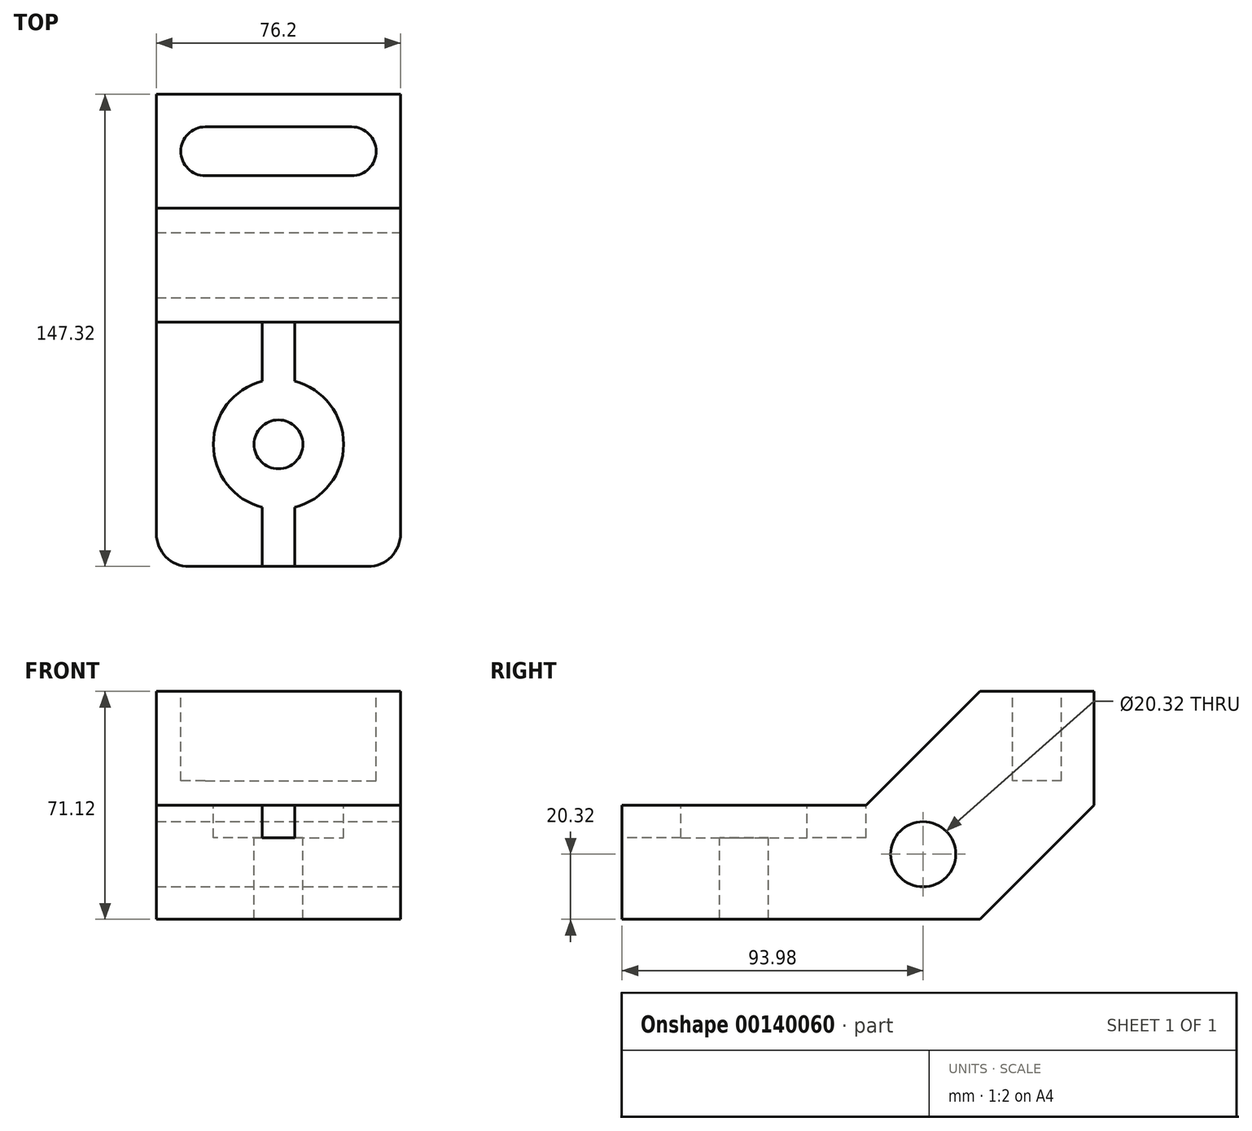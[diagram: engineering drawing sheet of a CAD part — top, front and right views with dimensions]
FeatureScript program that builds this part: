
annotation { "Feature Type Name" : "Feature", "Feature Type Description" : "" }
export const myFeature = defineFeature(function(context is Context, id is Id, definition is map)
    precondition{}
    {
        {
            var Q0;
            Q0=qCreatedBy(makeId("Right.planeOp"),FACE);
            var sketch = newSketch(context, id + "F0", { "sketchPlane" : qUnion([Q0])});
            skLineSegment(sketch, "E0", {"start": v(0, 0) * mm, "end": v(0, 35.56) * mm});
            skLineSegment(sketch, "E1", {"start": v(0, 35.56) * mm, "end": v(76.2, 35.56) * mm});
            skLineSegment(sketch, "E2", {"start": v(76.2, 35.56) * mm, "end": v(111.76, 71.12) * mm});
            skLineSegment(sketch, "E3", {"start": v(111.76, 71.12) * mm, "end": v(147.32, 71.12) * mm});
            skLineSegment(sketch, "E4", {"start": v(147.32, 71.12) * mm, "end": v(147.32, 35.56) * mm});
            skLineSegment(sketch, "E5", {"start": v(147.32, 35.56) * mm, "end": v(111.76, 0) * mm});
            skLineSegment(sketch, "E6", {"start": v(111.76, 0) * mm, "end": v(0, 0) * mm});
            skSolve(sketch);
        }
        {
            var Q0;
            Q0 = qSketchRegion(id + "F0", true);
            extrude(context, id + "F1", {"entities" : qUnion([Q0]), "depth" : 76.2 * mm});
        }
        {
            var Q0;
            Q0=makeQuery(id+"F1.opExtrude","CAP_FACE",FACE,{"disambiguationData":[OSD([sQuery(id+"F0.wireOp",EDGE,"E0"),sQuery(id+"F0.wireOp",EDGE,"E1"),sQuery(id+"F0.wireOp",EDGE,"E2"),sQuery(id+"F0.wireOp",EDGE,"E3"),sQuery(id+"F0.wireOp",EDGE,"E4"),sQuery(id+"F0.wireOp",EDGE,"E5"),sQuery(id+"F0.wireOp",EDGE,"E6")])],"isStart":false});
            var sketch = newSketch(context, id + "F2", { "sketchPlane" : qUnion([Q0])});
            skCircle(sketch, "E7", {"center": v(93.98, 20.32) * mm, "radius": 10.16 * mm});
            skSolve(sketch);
        }
        {
            var Q0;
            Q0 = qSketchRegion(id + "F2", true);
            extrude(context, id + "F3", {"entities" : qUnion([Q0]), "operationType" : NewBodyOperationType.REMOVE, "endBound" : BoundingType.THROUGH_ALL, "oppositeDirection" : true, "depth" : 25.4 * mm});
        }
        {
            var Q0;
            Q0=makeQuery(id+"F1.opExtrude","SWEPT_FACE",FACE,{"disambiguationData":[OSD([sQuery(id+"F0.wireOp",EDGE,"E3")])]});
            var sketch = newSketch(context, id + "F4", { "sketchPlane" : qUnion([Q0])});
            skLineSegment(sketch, "E8", {"start": v(15.24, 137.16) * mm, "end": v(60.96, 137.16) * mm});
            skArc(sketch, "E9", {"start": v(15.24, 137.16) * mm, "mid": v(7.62, 129.54) * mm, "end": v(15.24, 121.92) * mm});
            skLineSegment(sketch, "E10", {"start": v(15.24, 121.92) * mm, "end": v(60.96, 121.92) * mm});
            skArc(sketch, "E11", {"start": v(60.96, 121.92) * mm, "mid": v(68.58, 129.54) * mm, "end": v(60.96, 137.16) * mm});
            skSolve(sketch);
        }
        {
            var Q0;
            Q0 = qSketchRegion(id + "F4", true);
            extrude(context, id + "F5", {"entities" : qUnion([Q0]), "operationType" : NewBodyOperationType.REMOVE, "oppositeDirection" : true, "depth" : 27.94 * mm});
        }
        {
            var Q0;
            {var subQ1=sQuery(id+"F0.wireOp",EDGE,"E1");Q0=makeQuery(id+"F10.boolean.opBoolean","SPLIT",FACE,{"disambiguationData":[TD([makeQuery(id+"F10.opExtrude","SWEPT_FACE",FACE,{"disambiguationData":[OSD([sQuery(id+"F9.wireOp",EDGE,"E13.left")])]})])],"derivedFrom":makeQuery(id+"F1.opExtrude","SWEPT_FACE",FACE,{"disambiguationData":[OSD([subQ1])]})});}
            cPlane(context, id + "F6", {"entities" : qUnion([Q0]), "cplaneType" : CPlaneType.OFFSET, "offset" : 0 * mm, "width" : 152.4 * mm, "height" : 152.4 * mm});
        }
        {
            var Q0;
            Q0=qCreatedBy(id+"F6.planeOp",FACE);
            var sketch = newSketch(context, id + "F7", { "sketchPlane" : qUnion([Q0])});
            skPoint(sketch, "E12", {"position": v(38.1, 38.1) * mm});
            skSolve(sketch);
        }
        {
            var Q0;
            Q0=sQuery(id+"F7.wireOp",VERTEX,"E12");
            var Q1;
            Q1=makeQuery(id+"F1.opExtrude","SWEPT_BODY",BODY,{"disambiguationData":[OSD([sQuery(id+"F0.wireOp",EDGE,"E0"),sQuery(id+"F0.wireOp",EDGE,"E1"),sQuery(id+"F0.wireOp",EDGE,"E2"),sQuery(id+"F0.wireOp",EDGE,"E3"),sQuery(id+"F0.wireOp",EDGE,"E4"),sQuery(id+"F0.wireOp",EDGE,"E5"),sQuery(id+"F0.wireOp",EDGE,"E6")])]});
            hole(context, id + "F8", {"style" : HoleStyle.C_BORE, "endStyle" : HoleEndStyle.THROUGH, "holeDiameter" : 15.24 * mm, "cBoreDiameter" : 40.64 * mm, "cBoreDepth" : 10.16 * mm, "locations" : qUnion([Q0]), "scope" : qUnion([Q1]), "isTappedThrough" : true});
        }
        {
            var Q0;
            Q0=makeQuery(id+"F1.opExtrude","SWEPT_FACE",FACE,{"disambiguationData":[OSD([sQuery(id+"F0.wireOp",EDGE,"E1")])]});
            var sketch = newSketch(context, id + "F9", { "sketchPlane" : qUnion([Q0])});
            skLineSegment(sketch, "E13.bottom", {"start": v(33.02, 76.2) * mm, "end": v(43.18, 76.2) * mm});
            skLineSegment(sketch, "E13.top", {"start": v(33.02, 0) * mm, "end": v(43.18, 0) * mm});
            skLineSegment(sketch, "E13.left", {"start": v(33.02, 76.2) * mm, "end": v(33.02, 0) * mm});
            skLineSegment(sketch, "E13.right", {"start": v(43.18, 76.2) * mm, "end": v(43.18, 0) * mm});
            skSolve(sketch);
        }
        {
            var Q0;
            Q0 = qSketchRegion(id + "F9", true);
            extrude(context, id + "F10", {"entities" : qUnion([Q0]), "operationType" : NewBodyOperationType.REMOVE, "oppositeDirection" : true, "depth" : 10.16 * mm});
        }
        {
            var Q0;
            Q0=makeQuery(id+"F1.opExtrude","CAP_EDGE",EDGE,{"disambiguationData":[OSD([sQuery(id+"F0.wireOp",EDGE,"E0")])],"isStart":false});
            var Q1;
            Q1=makeQuery(id+"F1.opExtrude","CAP_EDGE",EDGE,{"disambiguationData":[OSD([sQuery(id+"F0.wireOp",EDGE,"E0")])],"isStart":true});
            fillet(context, id + "F11", {"entities" : qUnion([Q0, Q1]), "radius" : 10.16 * mm, "tangentPropagation" : true, "allowEdgeOverflow" : false});
        }
    });
